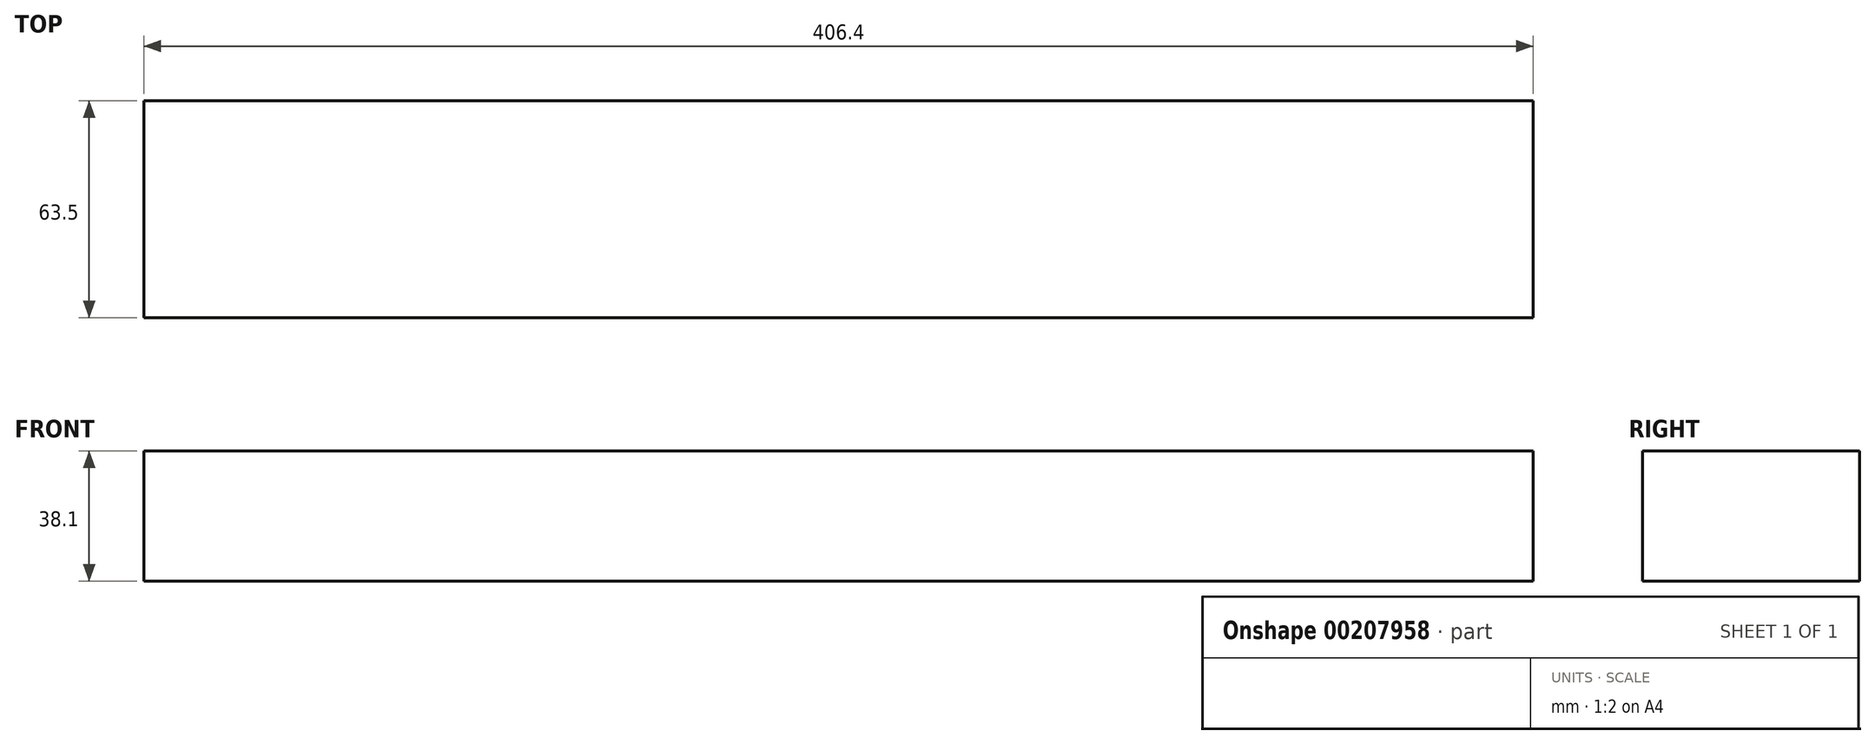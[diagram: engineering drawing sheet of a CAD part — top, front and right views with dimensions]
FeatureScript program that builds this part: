
annotation { "Feature Type Name" : "Feature", "Feature Type Description" : "" }
export const myFeature = defineFeature(function(context is Context, id is Id, definition is map)
    precondition{}
    {
        {
            var Q0;
            Q0=qCreatedBy(makeId("Right.planeOp"),FACE);
            var sketch = newSketch(context, id + "F0", { "sketchPlane" : qUnion([Q0])});
            skLineSegment(sketch, "E0.bottom", {"start": v(0, 0) * mm, "end": v(63.5, 0) * mm});
            skLineSegment(sketch, "E0.top", {"start": v(0, 38.1) * mm, "end": v(63.5, 38.1) * mm});
            skLineSegment(sketch, "E0.left", {"start": v(0, 0) * mm, "end": v(0, 38.1) * mm});
            skLineSegment(sketch, "E0.right", {"start": v(63.5, 0) * mm, "end": v(63.5, 38.1) * mm});
            skSolve(sketch);
        }
        {
            var Q0;
            Q0=qSketchRegion(id+"F0",true);
            extrude(context, id + "F1", {"entities" : qUnion([Q0]), "depth" : 406.4 * mm});
        }
    });
